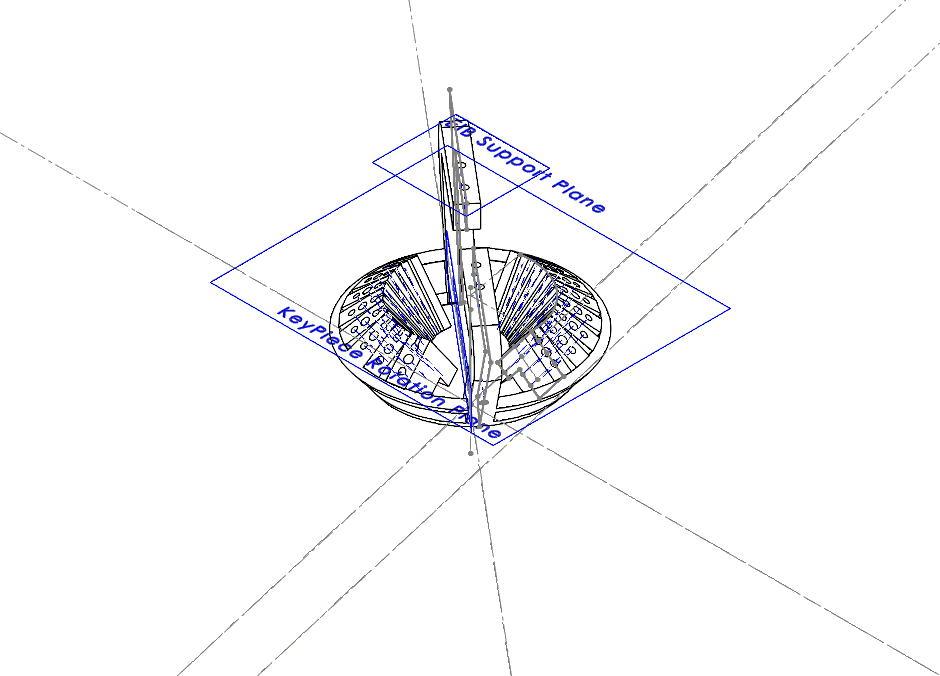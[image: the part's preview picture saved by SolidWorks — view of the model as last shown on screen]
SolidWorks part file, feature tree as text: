
SOLIDWORKS PART (.sldprt)
format: sldprt  version: not decoded by parser v0  size: 872,960 bytes
history: native  units: mm
features: sketch x13, cut_extrude x5, extrude x3, plane x3, material x1, revolve x1, mirror x1, fillet x1 (+12 scaffold rows collapsed)
feature tree (40):
  scaffold x12  (default folders/planes/origin — collapsed)
  material  "Material <not specified>"
  sketch  "Sketch3"
  sketch  "Sketch1"  dims[c1.D1=10.0mm c1.D2=7.0mm c1.D3=1.5mm c1.D4=1.0mm c1.D5=4.5mm c1.D6=1.75mm c1.D7=3.5mm c1.D8=3.0mm c1.D9=10.0mm c1.D10=~7.071068mm c1.D11=~785.398163mm c2.D6=1.75mm c2.D10=~10.985199mm c2.D11=~16.538672mm c2.D1=~263.580812mm]
  extrude  "KeyPiece"  Depth=1.5mm
  plane  "KeyPiece Rotation Plane"
  sketch  "KeyPiece Rotation Arc"  dims[c1.D1=~349.06585mm c1.D2=~349.06585mm c2.D1=~2792.526803mm]
  sketch  "ConeInside"  dims[c1.D1=7.0mm c2.D1=8.0 c2.D3=10.0mm c2.D2=1.0 c2.D4=10.0mm]
  sketch  "Sketch27"  dims[D1=0.0mm]
  cut_extrude  "TubingHoles"  [1 undecoded]
  sketch  "Sketch36"  dims[c1.D2=1.0mm c1.D1=0.5mm c2.D2=1.5mm]
  cut_extrude  "30gSlot"  [1 undecoded]
  sketch  "Sketch29"  dims[D1=1.5mm D2=1.5mm D3=1.5mm]
  revolve  "Revolve1"  [1 undecoded]
  sketch  "SupportPlaneAxis"  dims[D1=~1458.596589mm]
  extrude  "CrvPattern2"  Depth=8
  plane  "SupportPlane"
  mirror  "Mirror1"
  sketch  "Sketch30"  dims[c1.D1=20.0mm c1.D2=30.0mm c2.D1=27.0mm c2.D3=~785.398163mm c2.D2=25.0mm c2.D4=~698.131701mm c2.D5=~1570.796327mm c2.D6=~16.410183mm c3.D4=~698.131701mm c3.D1=5.0mm c3.D2=5.0mm c3.D3=4.0mm]
  extrude  "Boss-Extrude1"  Depth=1.75mm
  fillet  "Fillet1"  Radius=4mm
  plane  "EIB Support Plane"  Offset=0mm
  sketch  "Sketch35"  dims[D3=~3.30291mm D4=~2.618552mm D1=8.5mm D2=13.335mm]
  cut_extrude  "Cut-Extrude - Mounting Holes"  [1 undecoded]
  sketch  "Sketch37"  dims[D2=~1.822063mm D1=~3.857774mm]
  cut_extrude  "Cut-Extrude2"  [1 undecoded]
  sketch  "Sketch38"  dims[D1=~4.497392mm]
  cut_extrude  "Cut-Extrude3"  [1 undecoded]
  sketch  "Sketch34"  dims[D1=~6283.185307mm D3=10.0mm D4=1.0mm D7=0.0mm]
decode coverage: 16 of 24 modeling features carry decoded parameters
note: ~ marks probable driven/reference dimensions
note: 6 parameter values undecoded
summary: no parameter record found for 6 features
note: suppression state not decoded; provenance and decode notes live in map.json
